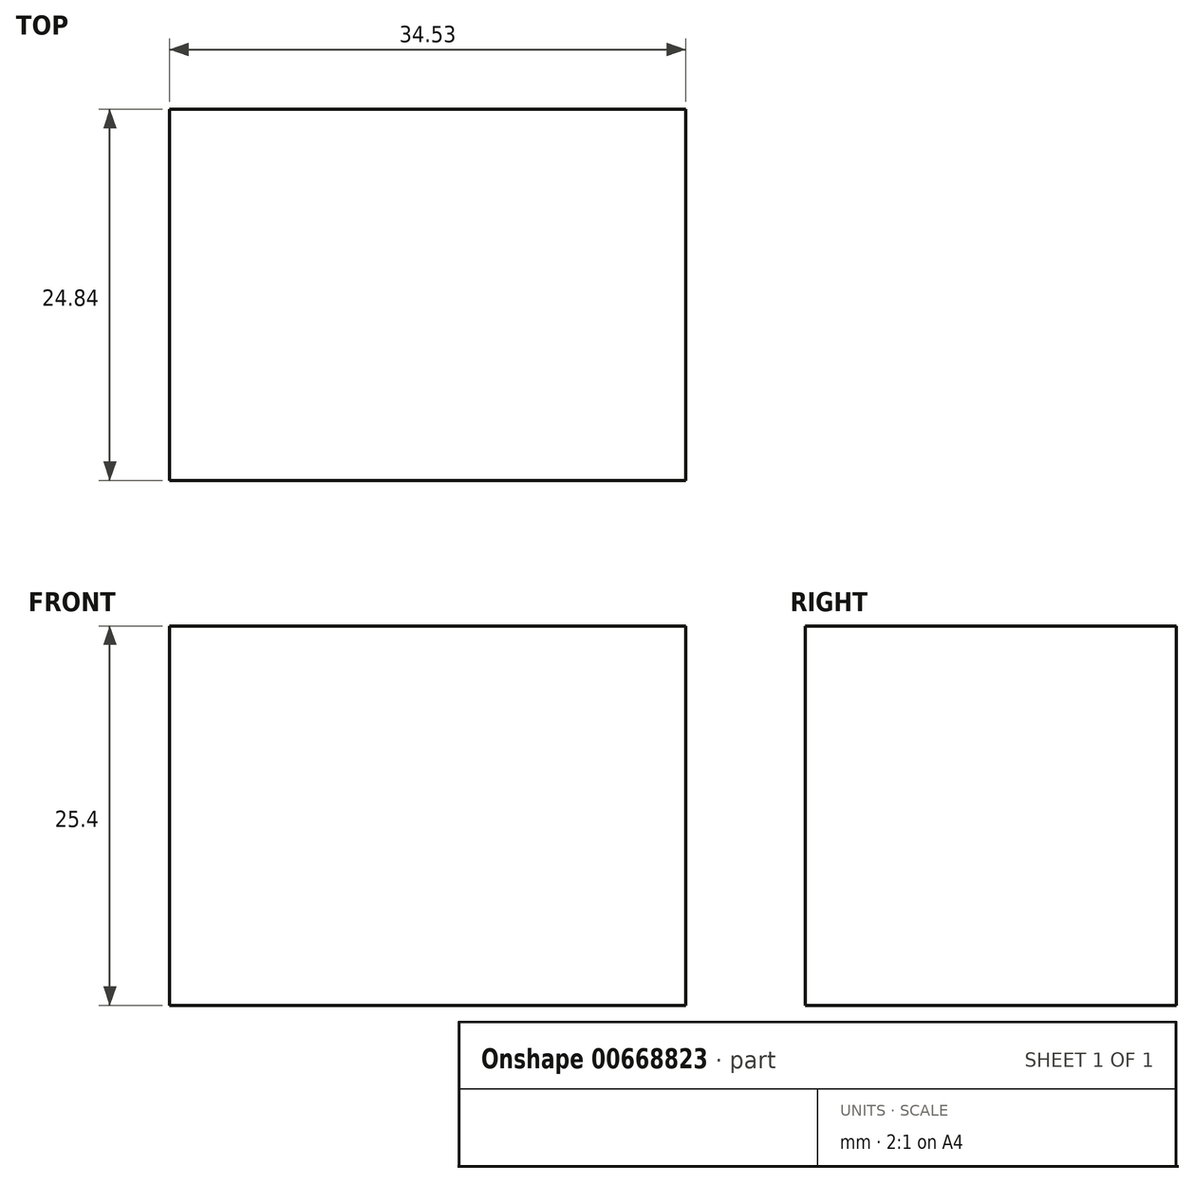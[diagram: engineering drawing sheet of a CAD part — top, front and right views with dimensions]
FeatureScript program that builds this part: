
annotation { "Feature Type Name" : "Feature", "Feature Type Description" : "" }
export const myFeature = defineFeature(function(context is Context, id is Id, definition is map)
    precondition{}
    {
        {
            var Q0;
            Q0=qCreatedBy(makeId("Top.planeOp"),FACE);
            var sketch = newSketch(context, id + "F0", { "sketchPlane" : qUnion([Q0])});
            skLineSegment(sketch, "E0.bottom", {"start": v(0, 0) * mm, "end": v(34.53, 0) * mm});
            skLineSegment(sketch, "E0.top", {"start": v(0, 24.84) * mm, "end": v(34.53, 24.84) * mm});
            skLineSegment(sketch, "E0.left", {"start": v(0, 0) * mm, "end": v(0, 24.84) * mm});
            skLineSegment(sketch, "E0.right", {"start": v(34.53, 0) * mm, "end": v(34.53, 24.84) * mm});
            skSolve(sketch);
        }
        {
            var Q0;
            Q0=makeQuery(id+"F0.imprint","IMPRINT",FACE,{"disambiguationData":[TD([[makeQuery(id+"F0.imprint","IMPRINT",EDGE,{"derivedFrom":sQuery(id+"F0.wireOp",EDGE,"E0.bottom")}),1.0]])]});
            extrude(context, id + "F1", {"entities" : qUnion([Q0]), "depth" : 25.4 * mm, "offsetDistance" : 25.4 * mm});
        }
    });
